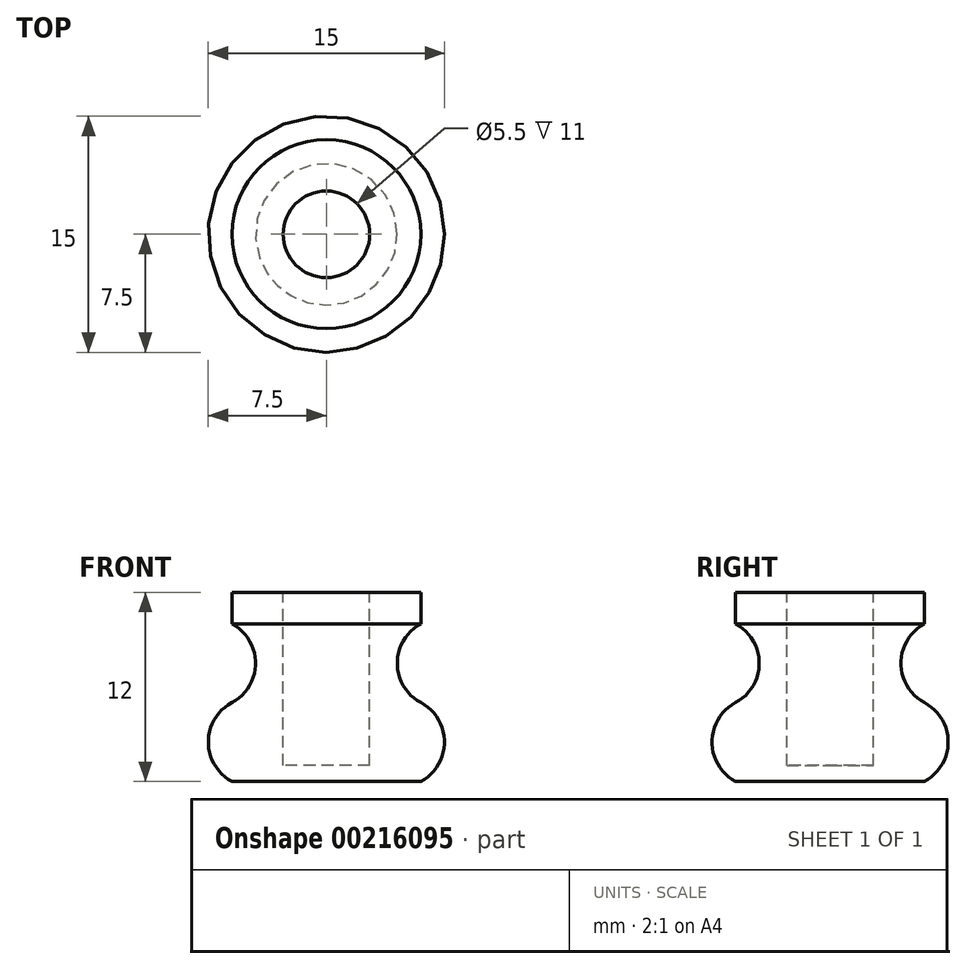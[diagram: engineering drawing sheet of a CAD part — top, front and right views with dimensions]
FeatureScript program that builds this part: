
annotation { "Feature Type Name" : "Feature", "Feature Type Description" : "" }
export const myFeature = defineFeature(function(context is Context, id is Id, definition is map)
    precondition{}
    {
        {
            var Q0;
            Q0=qCreatedBy(makeId("Front.planeOp"),FACE);
            var sketch = newSketch(context, id + "F0", { "sketchPlane" : qUnion([Q0])});
            skLineSegment(sketch, "E0", {"start": v(0, 0) * mm, "end": v(6, 0) * mm});
            skArc(sketch, "E1", {"start": v(6, 0) * mm, "mid": v(7.5, 2.5) * mm, "end": v(6, 5) * mm});
            skArc(sketch, "E2", {"start": v(6, 10) * mm, "mid": v(4.5, 7.5) * mm, "end": v(6, 5) * mm});
            skLineSegment(sketch, "E3", {"start": v(6, 10) * mm, "end": v(6, 12) * mm});
            skLineSegment(sketch, "E4", {"start": v(6, 12) * mm, "end": v(2.75, 12) * mm});
            skLineSegment(sketch, "E5", {"start": v(2.75, 12) * mm, "end": v(2.75, 1) * mm});
            skLineSegment(sketch, "E6", {"start": v(2.75, 1) * mm, "end": v(0, 1) * mm});
            skLineSegment(sketch, "E7", {"start": v(0, 1) * mm, "end": v(0, 0) * mm});
            skSolve(sketch);
        }
        {
            var Q0;
            Q0=makeQuery(id+"F0.imprint","IMPRINT",FACE,{"disambiguationData":[TD([[makeQuery(id+"F0.imprint","IMPRINT",EDGE,{"derivedFrom":sQuery(id+"F0.wireOp",EDGE,"E0")}),1.0]])]});
            var Q1;
            Q1=sQuery(id+"F0.wireOp",EDGE,"E7");
            revolve(context, id + "F1", {"entities" : qUnion([Q0]), "axis" : qUnion([Q1]), "revolveType" : RevolveType.FULL});
        }
    });
